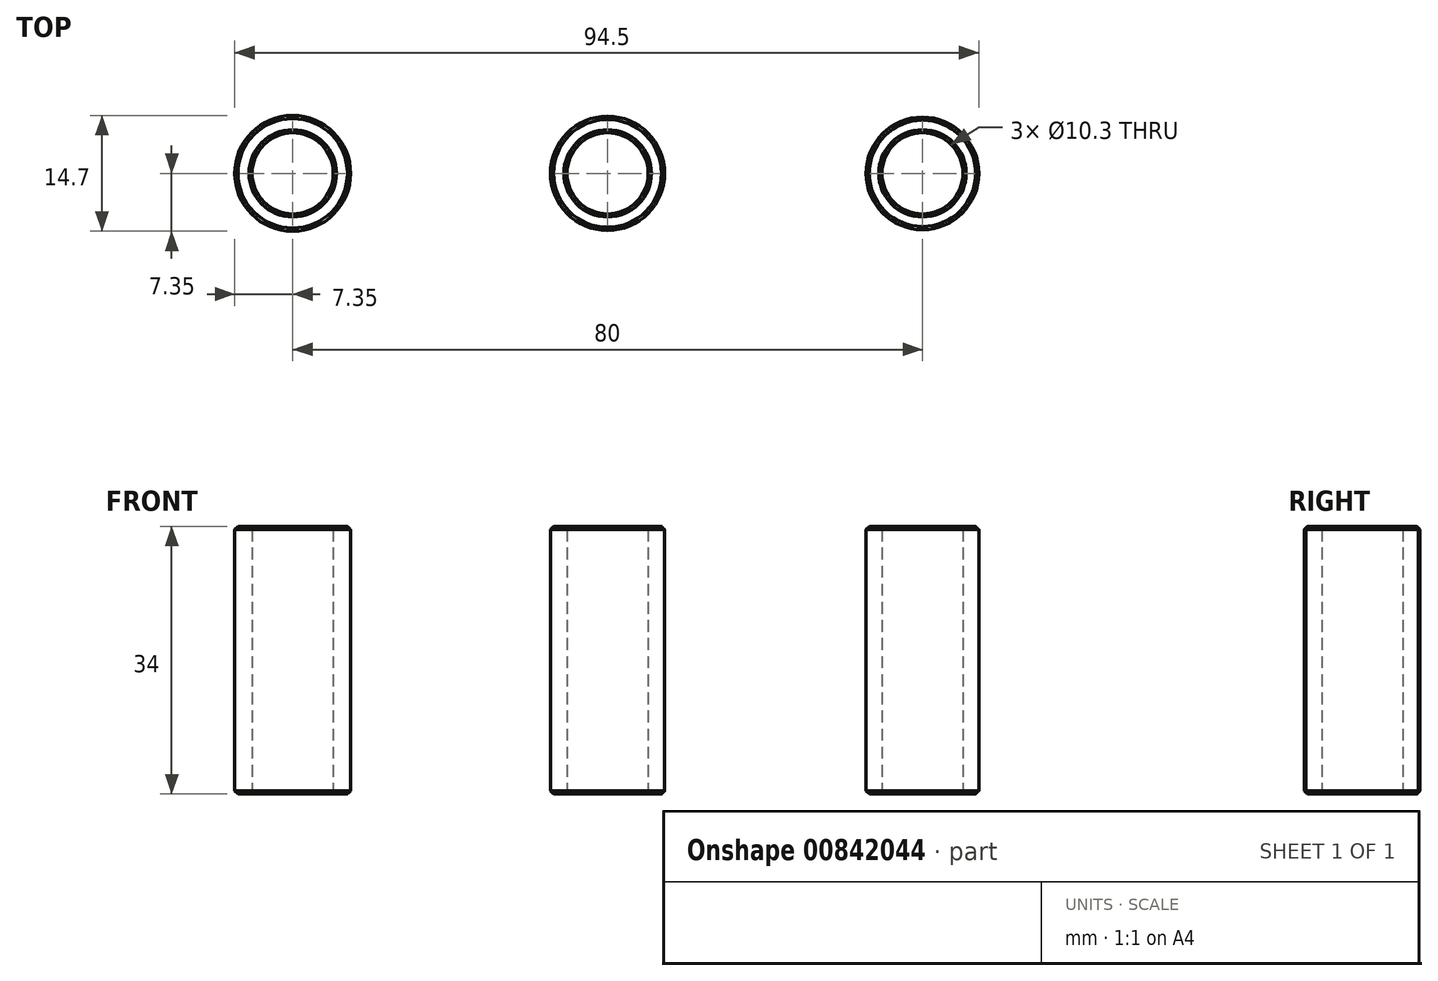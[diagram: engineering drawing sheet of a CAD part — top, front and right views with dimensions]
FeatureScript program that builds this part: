
annotation { "Feature Type Name" : "Feature", "Feature Type Description" : "" }
export const myFeature = defineFeature(function(context is Context, id is Id, definition is map)
    precondition{}
    {
        {
            var Q0;
            Q0=qCreatedBy(makeId("Top.planeOp"),FACE);
            var sketch = newSketch(context, id + "F0", { "sketchPlane" : qUnion([Q0])});
            skCircle(sketch, "E0", {"center": v(0, 0) * mm, "radius": 7.25 * mm});
            skCircle(sketch, "E1", {"center": v(0, 0) * mm, "radius": 5.15 * mm});
            skCircle(sketch, "E2", {"center": v(-40, 0) * mm, "radius": 7.35 * mm});
            skCircle(sketch, "E3", {"center": v(-40, 0) * mm, "radius": 5.15 * mm});
            skCircle(sketch, "E4", {"center": v(40, 0) * mm, "radius": 7.15 * mm});
            skCircle(sketch, "E5", {"center": v(40, 0) * mm, "radius": 5.15 * mm});
            skSolve(sketch);
        }
        {
            var Q0;
            Q0 = qSketchRegion(id + "F0", true);
            extrude(context, id + "F1", {"entities" : qUnion([Q0]), "depth" : 34 * mm, "offsetDistance" : 25 * mm});
        }
        {
            var Q0;
            Q0=makeQuery(id+"F1.opExtrude","CAP_EDGE",EDGE,{"disambiguationData":[OSD([sQuery(id+"F0.wireOp",EDGE,"E0")])],"isStart":true});
            var Q1;
            Q1=makeQuery(id+"F1.opExtrude","CAP_EDGE",EDGE,{"disambiguationData":[OSD([sQuery(id+"F0.wireOp",EDGE,"E2")])],"isStart":true});
            var Q2;
            Q2=makeQuery(id+"F1.opExtrude","CAP_EDGE",EDGE,{"disambiguationData":[OSD([sQuery(id+"F0.wireOp",EDGE,"E3")])],"isStart":true});
            var Q3;
            Q3=makeQuery(id+"F1.opExtrude","CAP_EDGE",EDGE,{"disambiguationData":[OSD([sQuery(id+"F0.wireOp",EDGE,"E4")])],"isStart":true});
            var Q4;
            Q4=makeQuery(id+"F1.opExtrude","CAP_EDGE",EDGE,{"disambiguationData":[OSD([sQuery(id+"F0.wireOp",EDGE,"E5")])],"isStart":true});
            var Q5;
            Q5=makeQuery(id+"F1.opExtrude","CAP_EDGE",EDGE,{"disambiguationData":[OSD([sQuery(id+"F0.wireOp",EDGE,"E1")])],"isStart":true});
            chamfer(context, id + "F2", {"entities" : qUnion([Q0, Q1, Q2, Q3, Q4, Q5]), "width" : .4 * mm, "tangentPropagation" : true});
        }
        {
            var Q0;
            Q0=makeQuery(id+"F1.opExtrude","CAP_EDGE",EDGE,{"disambiguationData":[OSD([sQuery(id+"F0.wireOp",EDGE,"E0")])],"isStart":false});
            var Q1;
            Q1=makeQuery(id+"F1.opExtrude","CAP_EDGE",EDGE,{"disambiguationData":[OSD([sQuery(id+"F0.wireOp",EDGE,"E2")])],"isStart":false});
            var Q2;
            Q2=makeQuery(id+"F1.opExtrude","CAP_EDGE",EDGE,{"disambiguationData":[OSD([sQuery(id+"F0.wireOp",EDGE,"E3")])],"isStart":false});
            var Q3;
            Q3=makeQuery(id+"F1.opExtrude","CAP_EDGE",EDGE,{"disambiguationData":[OSD([sQuery(id+"F0.wireOp",EDGE,"E4")])],"isStart":false});
            var Q4;
            Q4=makeQuery(id+"F1.opExtrude","CAP_EDGE",EDGE,{"disambiguationData":[OSD([sQuery(id+"F0.wireOp",EDGE,"E5")])],"isStart":false});
            var Q5;
            Q5=makeQuery(id+"F1.opExtrude","CAP_EDGE",EDGE,{"disambiguationData":[OSD([sQuery(id+"F0.wireOp",EDGE,"E1")])],"isStart":false});
            chamfer(context, id + "F3", {"entities" : qUnion([Q0, Q1, Q2, Q3, Q4, Q5]), "width" : .4 * mm, "tangentPropagation" : true});
        }
    });
